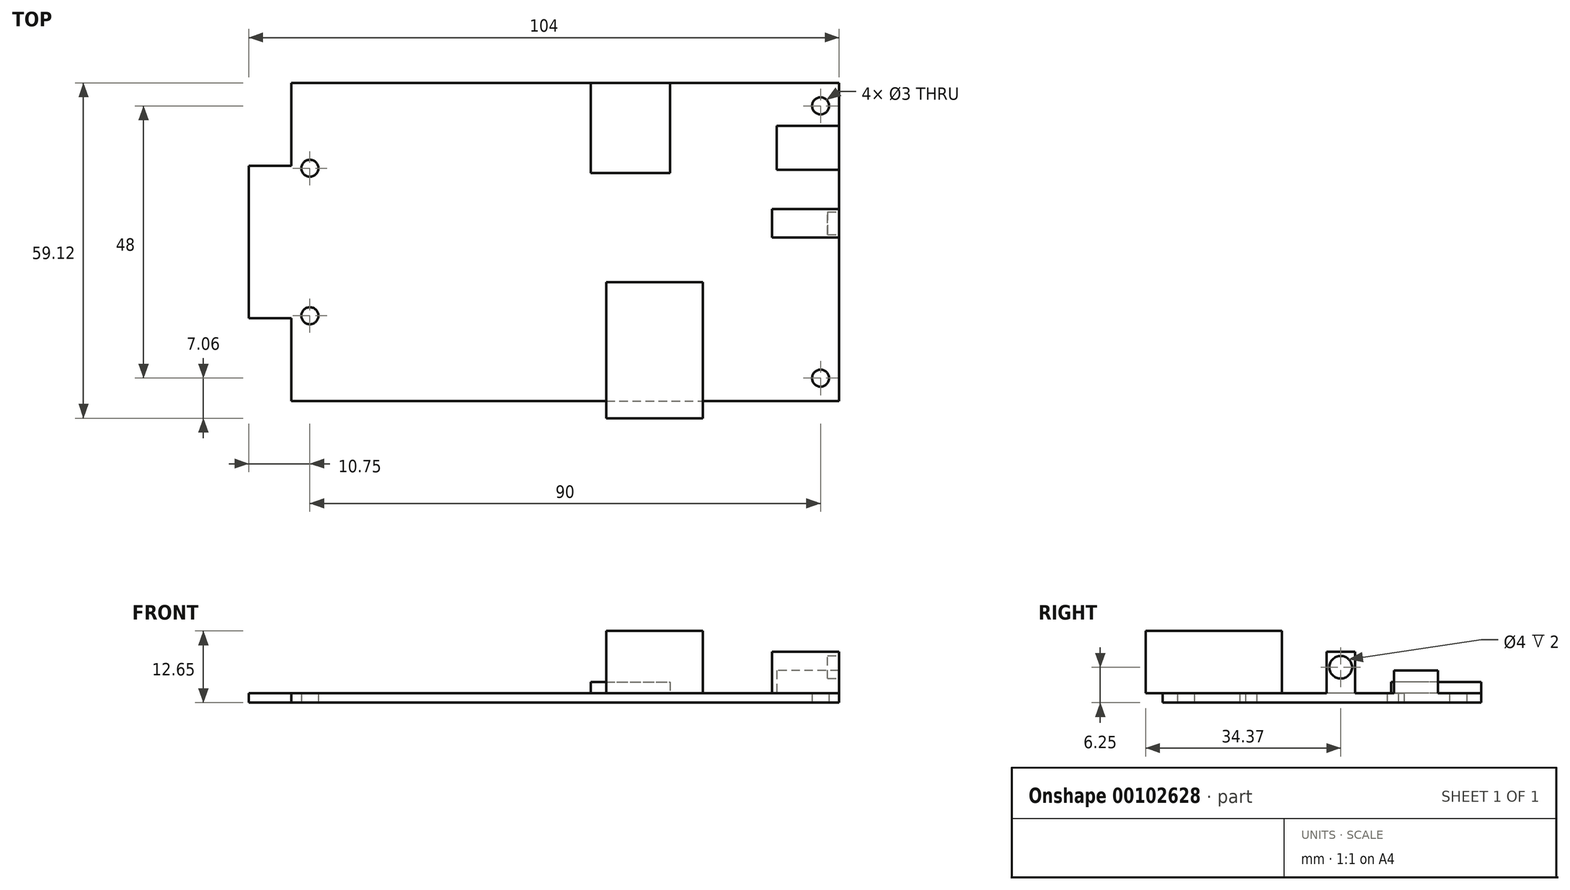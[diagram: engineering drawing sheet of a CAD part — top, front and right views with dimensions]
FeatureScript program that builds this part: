
annotation { "Feature Type Name" : "Feature", "Feature Type Description" : "" }
export const myFeature = defineFeature(function(context is Context, id is Id, definition is map)
    precondition{}
    {
        {
            var Q0;
            Q0=qCreatedBy(makeId("Top.planeOp"),FACE);
            var sketch = newSketch(context, id + "F0", { "sketchPlane" : qUnion([Q0])});
            skLineSegment(sketch, "E0.bottom", {"start": v(-48.25, 28.06) * mm, "end": v(48.25, 28.06) * mm});
            skLineSegment(sketch, "E0.left", {"start": v(-48.25, 28.06) * mm, "end": v(-48.25, 13.44) * mm});
            skLineSegment(sketch, "E1", {"start": v(-48.25, 13.44) * mm, "end": v(-55.75, 13.44) * mm});
            skLineSegment(sketch, "E2", {"start": v(48.25, 28.06) * mm, "end": v(48.25, 0) * mm});
            skLineSegment(sketch, "E3", {"start": v(-55.75, 13.44) * mm, "end": v(-55.75, 0) * mm});
            skLineSegment(sketch, "E4.MirrorCS", {"start": v(-55.75, -13.44) * mm, "end": v(-55.75, 0) * mm});
            skLineSegment(sketch, "E5.MirrorCS", {"start": v(48.25, -28.06) * mm, "end": v(48.25, 0) * mm});
            skLineSegment(sketch, "E6.MirrorCS", {"start": v(-48.25, -13.44) * mm, "end": v(-55.75, -13.44) * mm});
            skLineSegment(sketch, "E7.MirrorCS", {"start": v(-48.25, -28.06) * mm, "end": v(48.25, -28.06) * mm});
            skLineSegment(sketch, "E8.MirrorCS", {"start": v(-48.25, -28.06) * mm, "end": v(-48.25, -13.44) * mm});
            skCircle(sketch, "E9", {"center": v(-45, 13) * mm, "radius": 1.5 * mm});
            skCircle(sketch, "E10", {"center": v(45, 24) * mm, "radius": 1.5 * mm});
            skCircle(sketch, "E11.MirrorC", {"center": v(-45, -13) * mm, "radius": 1.5 * mm});
            skCircle(sketch, "E12.MirrorC", {"center": v(45, -24) * mm, "radius": 1.5 * mm});
            skLineSegment(sketch, "E13.bottom", {"start": v(48.25, 5.81) * mm, "end": v(36.45, 5.8) * mm});
            skLineSegment(sketch, "E13.top", {"start": v(48.25, 0.81) * mm, "end": v(36.45, 0.8) * mm});
            skLineSegment(sketch, "E13.left", {"start": v(48.25, 5.81) * mm, "end": v(48.25, 0.8) * mm});
            skLineSegment(sketch, "E13.right", {"start": v(36.45, 5.8) * mm, "end": v(36.45, 0.81) * mm});
            skLineSegment(sketch, "E14", {"start": v(36.45, 3.31) * mm, "end": v(48.25, 3.31) * mm, "construction": true});
            skLineSegment(sketch, "E15.bottom", {"start": v(4.39, 28.06) * mm, "end": v(18.59, 28.06) * mm});
            skLineSegment(sketch, "E15.top", {"start": v(4.39, 12.16) * mm, "end": v(18.59, 12.16) * mm});
            skLineSegment(sketch, "E15.left", {"start": v(4.39, 28.06) * mm, "end": v(4.4, 12.16) * mm});
            skLineSegment(sketch, "E15.right", {"start": v(18.59, 28.06) * mm, "end": v(18.59, 12.16) * mm});
            skLineSegment(sketch, "E16.bottom", {"start": v(36.45, 5.8) * mm, "end": v(48.25, 5.8) * mm});
            skLineSegment(sketch, "E16.top", {"start": v(36.45, 0.81) * mm, "end": v(48.25, 0.81) * mm});
            skLineSegment(sketch, "E17", {"start": v(11.49, 28.06) * mm, "end": v(11.49, 12.16) * mm, "construction": true});
            skSolve(sketch);
        }
        {
            var Q0;
            Q0 = qSketchRegion(id + "F0", true);
            extrude(context, id + "F1", {"entities" : qUnion([Q0]), "depth" : 1.65 * mm});
        }
        {
            var Q0;
            Q0=makeQuery(id+"F1.opExtrude","CAP_FACE",FACE,{"disambiguationData":[OSD([sQuery(id+"F0.wireOp",EDGE,"E0.bottom"),sQuery(id+"F0.wireOp",EDGE,"E0.left"),sQuery(id+"F0.wireOp",EDGE,"E1"),sQuery(id+"F0.wireOp",EDGE,"E2"),sQuery(id+"F0.wireOp",EDGE,"E3"),sQuery(id+"F0.wireOp",EDGE,"E4.MirrorCS"),sQuery(id+"F0.wireOp",EDGE,"E5.MirrorCS"),sQuery(id+"F0.wireOp",EDGE,"E6.MirrorCS"),sQuery(id+"F0.wireOp",EDGE,"E7.MirrorCS"),sQuery(id+"F0.wireOp",EDGE,"E8.MirrorCS"),sQuery(id+"F0.wireOp",EDGE,"E9"),sQuery(id+"F0.wireOp",EDGE,"E10"),sQuery(id+"F0.wireOp",EDGE,"E11.MirrorC"),sQuery(id+"F0.wireOp",EDGE,"E12.MirrorC")])],"isStart":false});
            var sketch = newSketch(context, id + "F2", { "sketchPlane" : qUnion([Q0])});
            skLineSegment(sketch, "E18.bottom", {"start": v(4.5, 28.06) * mm, "end": v(18.5, 28.06) * mm});
            skLineSegment(sketch, "E18.top", {"start": v(4.5, 12.16) * mm, "end": v(18.5, 12.16) * mm});
            skLineSegment(sketch, "E18.left", {"start": v(4.5, 28.06) * mm, "end": v(4.5, 12.16) * mm});
            skLineSegment(sketch, "E18.right", {"start": v(18.5, 28.06) * mm, "end": v(18.5, 12.16) * mm});
            skLineSegment(sketch, "E19.bottom", {"start": v(48.25, 20.46) * mm, "end": v(37.25, 20.46) * mm});
            skLineSegment(sketch, "E19.top", {"start": v(48.25, 12.72) * mm, "end": v(37.25, 12.72) * mm});
            skLineSegment(sketch, "E19.left", {"start": v(48.25, 20.46) * mm, "end": v(48.25, 12.72) * mm});
            skLineSegment(sketch, "E19.right", {"start": v(37.25, 20.46) * mm, "end": v(37.25, 12.72) * mm});
            skLineSegment(sketch, "E20.bottom", {"start": v(7.25, -7.06) * mm, "end": v(24.25, -7.06) * mm});
            skLineSegment(sketch, "E20.top", {"start": v(7.25, -31.06) * mm, "end": v(24.25, -31.06) * mm});
            skLineSegment(sketch, "E20.left", {"start": v(7.25, -7.06) * mm, "end": v(7.25, -31.06) * mm});
            skLineSegment(sketch, "E20.right", {"start": v(24.25, -7.06) * mm, "end": v(24.25, -31.06) * mm});
            skLineSegment(sketch, "E21", {"start": v(15.75, -7.06) * mm, "end": v(15.75, -31.06) * mm, "construction": true});
            skSolve(sketch);
        }
        {
            var Q0;
            Q0=makeQuery(id+"F2.imprint","IMPRINT",FACE,{"disambiguationData":[TD([[makeQuery(id+"F2.imprint","IMPRINT",EDGE,{"derivedFrom":sQuery(id+"F2.wireOp",EDGE,"E18.bottom")}),-1.0]])]});
            extrude(context, id + "F3", {"entities" : qUnion([Q0]), "operationType" : NewBodyOperationType.ADD, "depth" : 2 * mm});
        }
        {
            var Q0;
            Q0=makeQuery(id+"F2.imprint","IMPRINT",FACE,{"disambiguationData":[TD([[makeQuery(id+"F2.imprint","IMPRINT",EDGE,{"derivedFrom":sQuery(id+"F2.wireOp",EDGE,"E19.bottom")}),1.0]])]});
            extrude(context, id + "F4", {"entities" : qUnion([Q0]), "operationType" : NewBodyOperationType.ADD, "depth" : 4 * mm});
        }
        {
            var Q0;
            {var subQ0=sQuery(id+"F2.wireOp",EDGE,"E20.bottom");Q0=makeQuery(id+"F2.imprint","IMPRINT",FACE,{"disambiguationData":[TD([[makeQuery(id+"F2.imprint","IMPRINT",EDGE,{"derivedFrom":subQ0}),-1.0]])]});}
            var Q1;
            {var subQ0=sQuery(id+"F2.wireOp",EDGE,"E20.top");Q1=makeQuery(id+"F2.imprint","IMPRINT",FACE,{"disambiguationData":[TD([[makeQuery(id+"F2.imprint","IMPRINT",EDGE,{"derivedFrom":subQ0}),1.0]])]});}
            extrude(context, id + "F5", {"entities" : qUnion([Q0, Q1]), "operationType" : NewBodyOperationType.ADD, "depth" : 11 * mm});
        }
        {
            var Q0;
            Q0=makeQuery(id+"F1.opExtrude","CAP_FACE",FACE,{"disambiguationData":[OSD([sQuery(id+"F0.wireOp",EDGE,"E0.bottom"),sQuery(id+"F0.wireOp",EDGE,"E0.left"),sQuery(id+"F0.wireOp",EDGE,"E1"),sQuery(id+"F0.wireOp",EDGE,"E2"),sQuery(id+"F0.wireOp",EDGE,"E3"),sQuery(id+"F0.wireOp",EDGE,"E4.MirrorCS"),sQuery(id+"F0.wireOp",EDGE,"E5.MirrorCS"),sQuery(id+"F0.wireOp",EDGE,"E6.MirrorCS"),sQuery(id+"F0.wireOp",EDGE,"E7.MirrorCS"),sQuery(id+"F0.wireOp",EDGE,"E8.MirrorCS"),sQuery(id+"F0.wireOp",EDGE,"E9"),sQuery(id+"F0.wireOp",EDGE,"E10"),sQuery(id+"F0.wireOp",EDGE,"E11.MirrorC"),sQuery(id+"F0.wireOp",EDGE,"E12.MirrorC"),sQuery(id+"F0.wireOp",EDGE,"E15.bottom"),sQuery(id+"F0.wireOp",EDGE,"E13.left")])],"isStart":false});
            var sketch = newSketch(context, id + "F6", { "sketchPlane" : qUnion([Q0])});
            skLineSegment(sketch, "E22.bottom", {"start": v(36.45, 5.8) * mm, "end": v(48.25, 5.8) * mm});
            skLineSegment(sketch, "E22.top", {"start": v(36.45, 0.81) * mm, "end": v(48.25, 0.81) * mm});
            skLineSegment(sketch, "E22.left", {"start": v(36.45, 5.8) * mm, "end": v(36.45, 0.81) * mm});
            skLineSegment(sketch, "E22.right", {"start": v(48.25, 5.81) * mm, "end": v(48.25, 0.81) * mm});
            skSolve(sketch);
        }
        {
            var Q0;
            Q0 = qSketchRegion(id + "F6", true);
            extrude(context, id + "F7", {"entities" : qUnion([Q0]), "operationType" : NewBodyOperationType.ADD, "depth" : 7.3 * mm});
        }
        {
            var Q0;
            Q0=makeQuery(id+"F7.boolean.opBoolean","MERGE",FACE,{"derivedFrom":[makeQuery(id+"F4.boolean.opBoolean","MERGE",FACE,{"derivedFrom":[makeQuery(id+"F1.opExtrude","SWEPT_FACE",FACE,{"disambiguationData":[OSD([sQuery(id+"F0.wireOp",EDGE,"E2"),sQuery(id+"F0.wireOp",EDGE,"E5.MirrorCS"),sQuery(id+"F0.wireOp",EDGE,"E13.left")])]}),makeQuery(id+"F4.opExtrude","SWEPT_FACE",FACE,{"disambiguationData":[OSD([sQuery(id+"F2.wireOp",EDGE,"E19.left")])]})]}),makeQuery(id+"F7.opExtrude","SWEPT_FACE",FACE,{"disambiguationData":[OSD([sQuery(id+"F6.wireOp",EDGE,"E22.right")])]})]});
            var sketch = newSketch(context, id + "F8", { "sketchPlane" : qUnion([Q0])});
            skCircle(sketch, "E23", {"center": v(3.3, 6.25) * mm, "radius": 2 * mm});
            skLineSegment(sketch, "E24", {"start": v(3.3, 8.95) * mm, "end": v(3.3, 6.25) * mm, "construction": true});
            skSolve(sketch);
        }
        {
            var Q0;
            Q0 = qSketchRegion(id + "F8", true);
            extrude(context, id + "F9", {"entities" : qUnion([Q0]), "operationType" : NewBodyOperationType.REMOVE, "oppositeDirection" : true, "depth" : 2 * mm});
        }
    });
